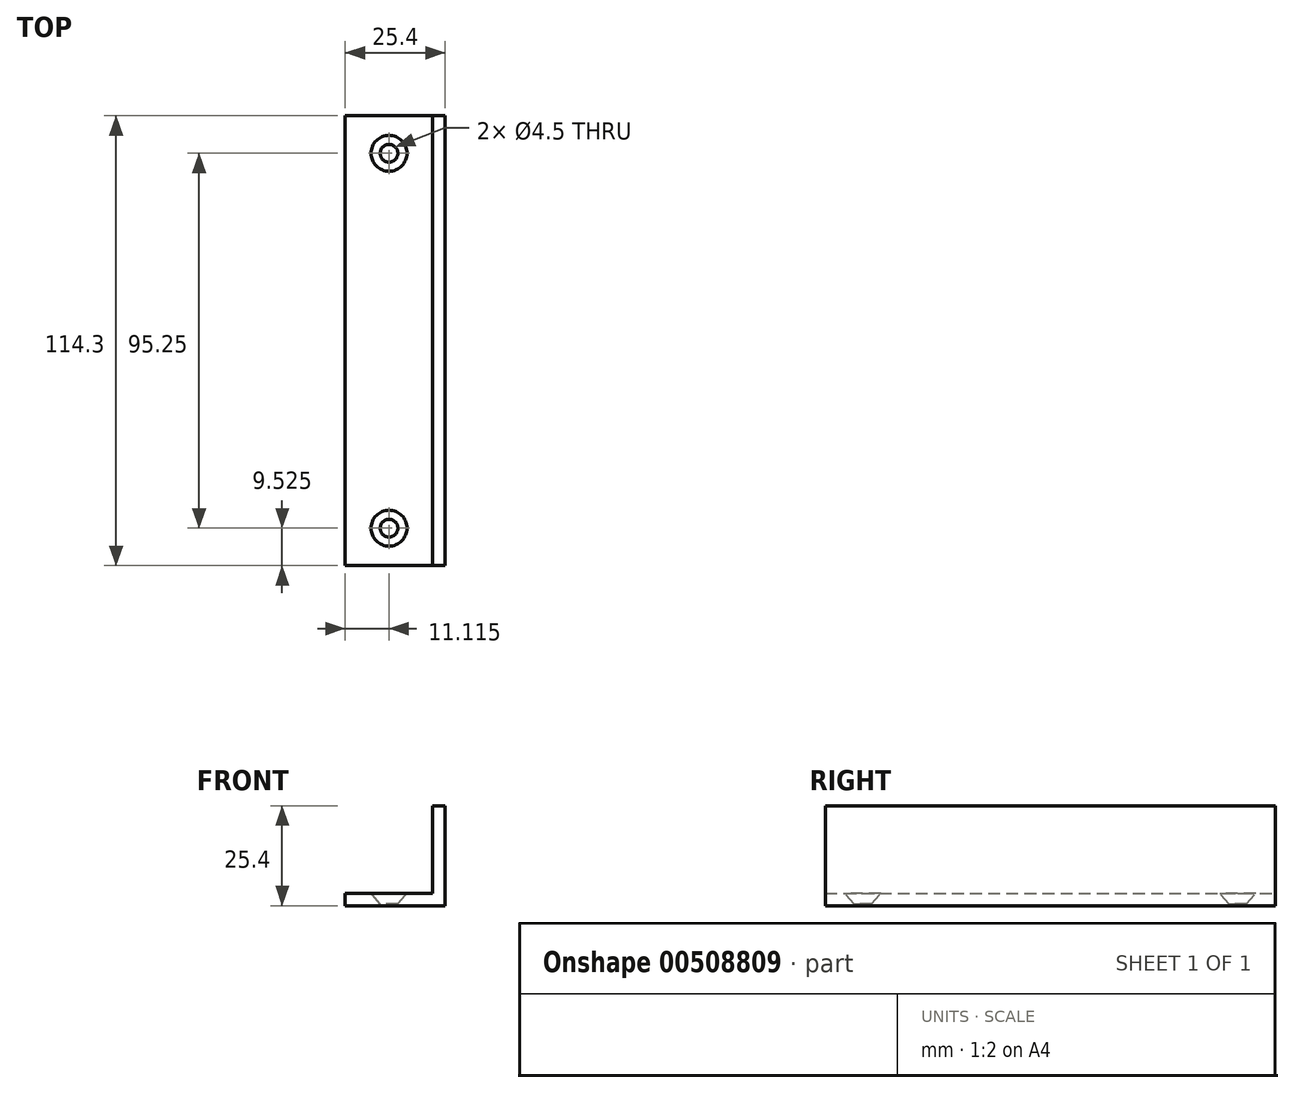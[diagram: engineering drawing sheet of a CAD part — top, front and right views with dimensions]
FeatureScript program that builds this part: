
annotation { "Feature Type Name" : "Feature", "Feature Type Description" : "" }
export const myFeature = defineFeature(function(context is Context, id is Id, definition is map)
    precondition{}
    {
        {
            var Q0;
            Q0=qCreatedBy(makeId("Front.planeOp"),FACE);
            var sketch = newSketch(context, id + "F0", { "sketchPlane" : qUnion([Q0])});
            skLineSegment(sketch, "E0.bottom", {"start": v(87.31, 25.4) * mm, "end": v(84.14, 25.4) * mm});
            skLineSegment(sketch, "E0.top", {"start": v(87.31, 0) * mm, "end": v(84.14, 0) * mm});
            skLineSegment(sketch, "E0.left", {"start": v(87.31, 25.4) * mm, "end": v(87.31, 0) * mm});
            skLineSegment(sketch, "E0.right", {"start": v(84.14, 25.4) * mm, "end": v(84.14, 0) * mm});
            skLineSegment(sketch, "E1.bottom", {"start": v(87.31, 0) * mm, "end": v(61.91, 0) * mm});
            skLineSegment(sketch, "E1.top", {"start": v(87.31, 3.18) * mm, "end": v(61.91, 3.18) * mm});
            skLineSegment(sketch, "E1.left", {"start": v(87.31, 0) * mm, "end": v(87.31, 3.17) * mm});
            skLineSegment(sketch, "E1.right", {"start": v(61.91, 0) * mm, "end": v(61.91, 3.17) * mm});
            skSolve(sketch);
        }
        {
            var Q0;
            Q0 = qSketchRegion(id + "F0", true);
            extrude(context, id + "F1", {"entities" : qUnion([Q0]), "depth" : 114.3 * mm, "offsetDistance" : 25.4 * mm});
        }
        {
            var Q0;
            Q0=makeQuery(id+"F1.opExtrude","SWEPT_FACE",FACE,{"disambiguationData":[OSD([sQuery(id+"F0.wireOp",EDGE,"E1.top")])]});
            var sketch = newSketch(context, id + "F2", { "sketchPlane" : qUnion([Q0])});
            skPoint(sketch, "E2", {"position": v(73.03, -9.53) * mm});
            skPoint(sketch, "E2.positionSnap0", {"position": v(73.03, 0) * mm});
            skPoint(sketch, "E3", {"position": v(73.03, -104.78) * mm});
            skSolve(sketch);
        }
        {
            var Q0;
            Q0=sQuery(id+"F2.wireOp",VERTEX,"E3");
            var Q1;
            Q1=sQuery(id+"F2.wireOp",VERTEX,"E2");
            var Q2;
            Q2=makeQuery(id+"F1.opExtrude","SWEPT_BODY",BODY,{"disambiguationData":[OSD([sQuery(id+"F0.wireOp",EDGE,"E0.bottom"),sQuery(id+"F0.wireOp",EDGE,"E0.left"),sQuery(id+"F0.wireOp",EDGE,"E0.right"),sQuery(id+"F0.wireOp",EDGE,"E1.bottom"),sQuery(id+"F0.wireOp",EDGE,"E1.top"),sQuery(id+"F0.wireOp",EDGE,"E1.left"),sQuery(id+"F0.wireOp",EDGE,"E1.right")])]});
            hole(context, id + "F3", {"style" : HoleStyle.C_SINK, "endStyle" : HoleEndStyle.THROUGH, "standardTappedOrClearance" : lookupTablePath({ "standard" : "ANSI", "fit" : "Normal (ASME)", "size" : "#8", "type" : "Clearance" }), "standardBlindInLast" : lookupTablePath({ "fit" : "Free", "standard" : "ANSI", "size" : "#8", "type" : "Clearance" }), "holeDiameter" : 4.5 * mm, "cSinkDiameter" : 9.12 * mm, "cSinkAngle" : 82 * degree, "isTappedThrough" : true, "tappedDepth" : 12.7 * mm, "tapClearance" : 3, "locations" : qUnion([Q0, Q1]), "scope" : qUnion([Q2])});
        }
    });
